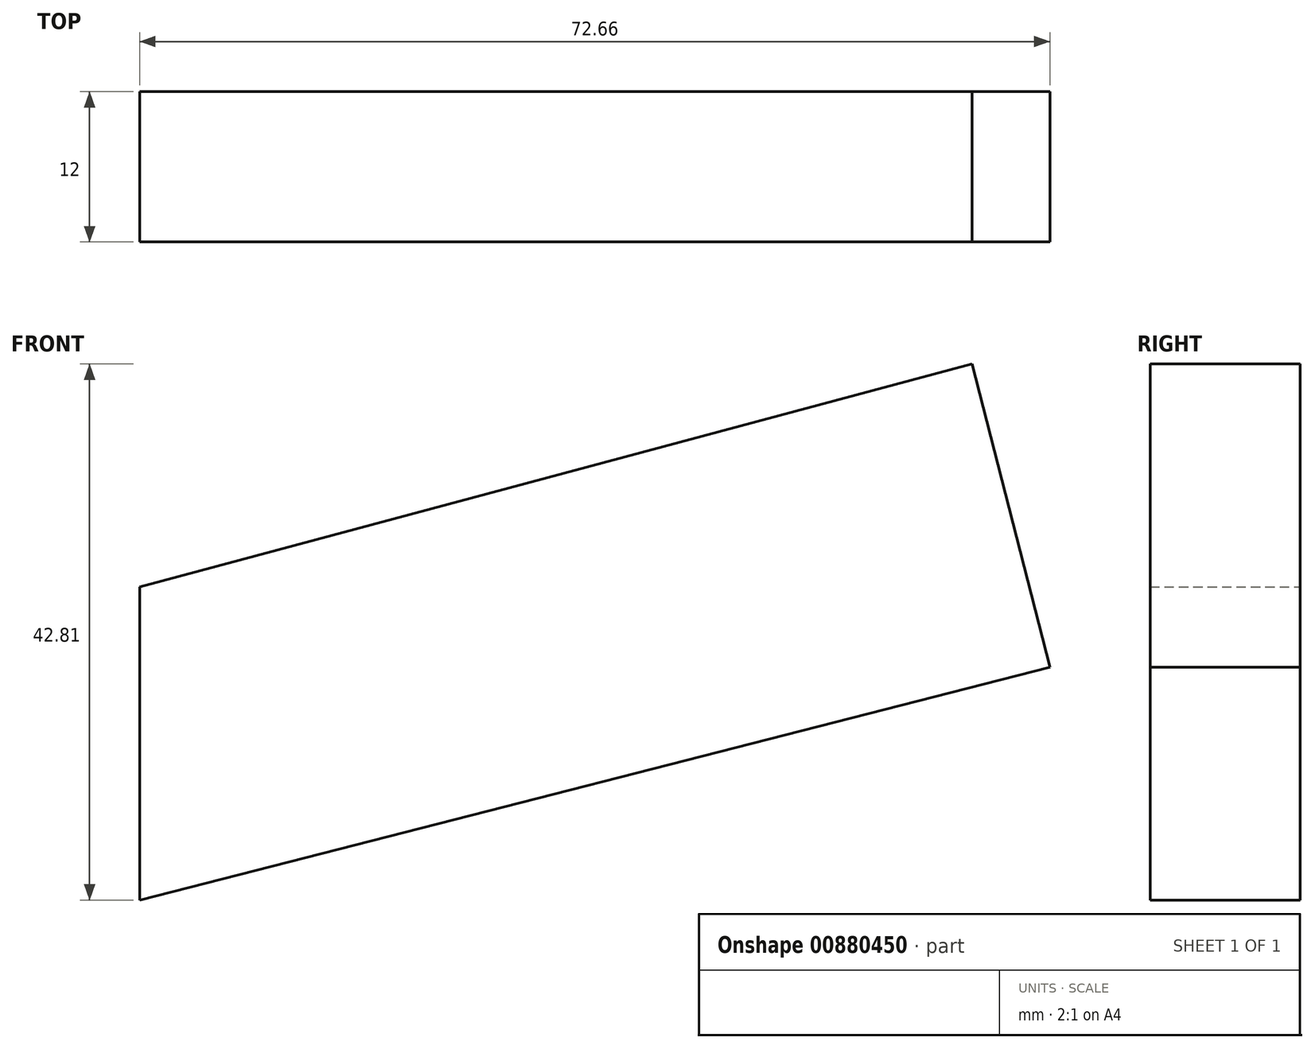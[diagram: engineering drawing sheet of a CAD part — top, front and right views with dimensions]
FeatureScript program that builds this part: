
annotation { "Feature Type Name" : "Feature", "Feature Type Description" : "" }
export const myFeature = defineFeature(function(context is Context, id is Id, definition is map)
    precondition{}
    {
        {
            var Q0;
            Q0=qCreatedBy(makeId("Front.planeOp"),FACE);
            var sketch = newSketch(context, id + "F0", { "sketchPlane" : qUnion([Q0])});
            skLineSegment(sketch, "E0", {"start": v(0, 0) * mm, "end": v(72.66, 18.59) * mm});
            skLineSegment(sketch, "E1", {"start": v(72.66, 18.59) * mm, "end": v(66.46, 42.8) * mm});
            skLineSegment(sketch, "E2", {"start": v(66.46, 42.8) * mm, "end": v(0, 25) * mm});
            skLineSegment(sketch, "E3", {"start": v(0, 25) * mm, "end": v(0, 0) * mm});
            skSolve(sketch);
        }
        {
            var Q0;
            Q0=makeQuery(id+"F0.imprint","IMPRINT",FACE,{"disambiguationData":[TD([[makeQuery(id+"F0.imprint","IMPRINT",EDGE,{"derivedFrom":sQuery(id+"F0.wireOp",EDGE,"E0")}),1.0]])]});
            extrude(context, id + "F1", {"entities" : qUnion([Q0]), "depth" : 12 * mm, "offsetDistance" : 25 * mm});
        }
    });
